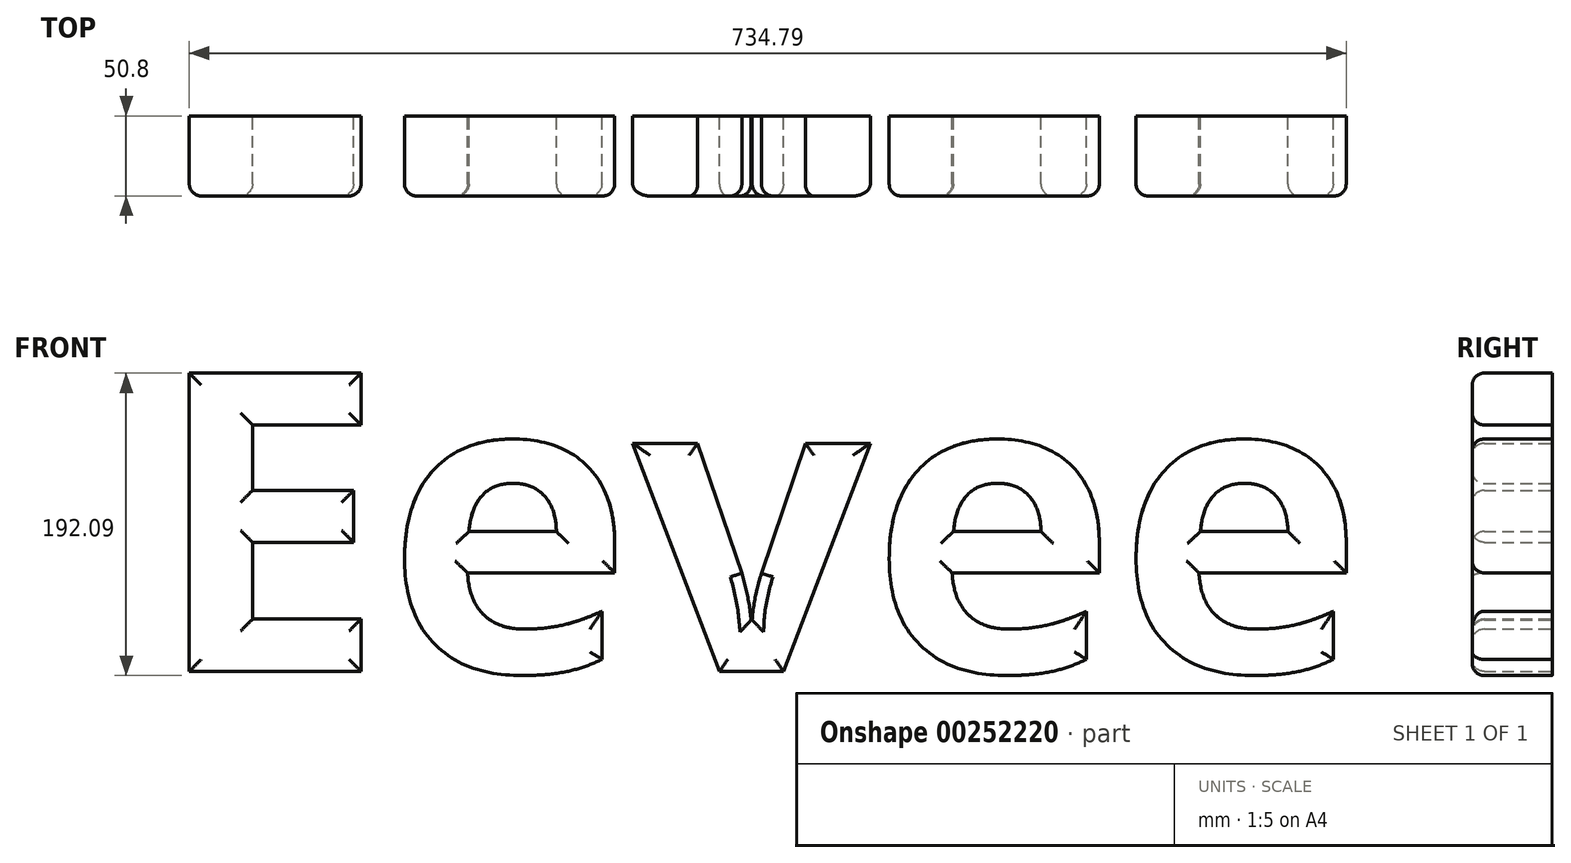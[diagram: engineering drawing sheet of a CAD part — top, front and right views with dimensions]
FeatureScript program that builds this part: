
annotation { "Feature Type Name" : "Feature", "Feature Type Description" : "" }
export const myFeature = defineFeature(function(context is Context, id is Id, definition is map)
    precondition{}
    {
        {
            var Q0;
            Q0=qCreatedBy(makeId("Front.planeOp"),FACE);
            var sketch = newSketch(context, id + "F0", { "sketchPlane" : qUnion([Q0])});
            skText(sketch, "E0", { "text": "Eevee", "fontName": "OpenSans-Bold.ttf"});
            const initialGuessF0  = {"E0": [-0.17, -0.0954, 1, 0, 0.1911]};
            skSetInitialGuess(sketch, initialGuessF0);
            skSolve(sketch);
        }
        {
            var Q0;
            Q0 = qSketchRegion(id + "F0", true);
            extrude(context, id + "F1", {"entities" : qUnion([Q0]), "depth" : 50.8 * mm});
        }
        {
            var Q0;
            Q0=makeQuery(id+"F1.opExtrude","CAP_FACE",FACE,{"disambiguationData":[OSD([sQuery(id+"F0.wireOp",EDGE,"E0.sketch_text.stroke-0"),sQuery(id+"F0.wireOp",EDGE,"E0.sketch_text.stroke-1"),sQuery(id+"F0.wireOp",EDGE,"E0.sketch_text.stroke-2"),sQuery(id+"F0.wireOp",EDGE,"E0.sketch_text.stroke-3"),sQuery(id+"F0.wireOp",EDGE,"E0.sketch_text.stroke-4"),sQuery(id+"F0.wireOp",EDGE,"E0.sketch_text.stroke-5"),sQuery(id+"F0.wireOp",EDGE,"E0.sketch_text.stroke-6"),sQuery(id+"F0.wireOp",EDGE,"E0.sketch_text.stroke-7"),sQuery(id+"F0.wireOp",EDGE,"E0.sketch_text.stroke-8"),sQuery(id+"F0.wireOp",EDGE,"E0.sketch_text.stroke-9"),sQuery(id+"F0.wireOp",EDGE,"E0.sketch_text.stroke-10"),sQuery(id+"F0.wireOp",EDGE,"E0.sketch_text.stroke-11")])],"isStart":false});
            var Q1;
            Q1=makeQuery(id+"F1.opExtrude","CAP_FACE",FACE,{"disambiguationData":[OSD([sQuery(id+"F0.wireOp",EDGE,"E0.sketch_text.stroke-12"),sQuery(id+"F0.wireOp",EDGE,"E0.sketch_text.stroke-13"),sQuery(id+"F0.wireOp",EDGE,"E0.sketch_text.stroke-14"),sQuery(id+"F0.wireOp",EDGE,"E0.sketch_text.stroke-15"),sQuery(id+"F0.wireOp",EDGE,"E0.sketch_text.stroke-16"),sQuery(id+"F0.wireOp",EDGE,"E0.sketch_text.stroke-17"),sQuery(id+"F0.wireOp",EDGE,"E0.sketch_text.stroke-18"),sQuery(id+"F0.wireOp",EDGE,"E0.sketch_text.stroke-19"),sQuery(id+"F0.wireOp",EDGE,"E0.sketch_text.stroke-20"),sQuery(id+"F0.wireOp",EDGE,"E0.sketch_text.stroke-21"),sQuery(id+"F0.wireOp",EDGE,"E0.sketch_text.stroke-22"),sQuery(id+"F0.wireOp",EDGE,"E0.sketch_text.stroke-23"),sQuery(id+"F0.wireOp",EDGE,"E0.sketch_text.stroke-24"),sQuery(id+"F0.wireOp",EDGE,"E0.sketch_text.stroke-25"),sQuery(id+"F0.wireOp",EDGE,"E0.sketch_text.stroke-26"),sQuery(id+"F0.wireOp",EDGE,"E0.sketch_text.stroke-27"),sQuery(id+"F0.wireOp",EDGE,"E0.sketch_text.stroke-28"),sQuery(id+"F0.wireOp",EDGE,"E0.sketch_text.stroke-29"),sQuery(id+"F0.wireOp",EDGE,"E0.sketch_text.stroke-30"),sQuery(id+"F0.wireOp",EDGE,"E0.sketch_text.stroke-31")])],"isStart":false});
            var Q2;
            Q2=makeQuery(id+"F1.opExtrude","CAP_FACE",FACE,{"disambiguationData":[OSD([sQuery(id+"F0.wireOp",EDGE,"E0.sketch_text.stroke-32"),sQuery(id+"F0.wireOp",EDGE,"E0.sketch_text.stroke-33"),sQuery(id+"F0.wireOp",EDGE,"E0.sketch_text.stroke-34"),sQuery(id+"F0.wireOp",EDGE,"E0.sketch_text.stroke-35"),sQuery(id+"F0.wireOp",EDGE,"E0.sketch_text.stroke-36"),sQuery(id+"F0.wireOp",EDGE,"E0.sketch_text.stroke-37"),sQuery(id+"F0.wireOp",EDGE,"E0.sketch_text.stroke-38"),sQuery(id+"F0.wireOp",EDGE,"E0.sketch_text.stroke-39"),sQuery(id+"F0.wireOp",EDGE,"E0.sketch_text.stroke-40"),sQuery(id+"F0.wireOp",EDGE,"E0.sketch_text.stroke-41")])],"isStart":false});
            var Q3;
            Q3=makeQuery(id+"F1.opExtrude","CAP_FACE",FACE,{"disambiguationData":[OSD([sQuery(id+"F0.wireOp",EDGE,"E0.sketch_text.stroke-42"),sQuery(id+"F0.wireOp",EDGE,"E0.sketch_text.stroke-43"),sQuery(id+"F0.wireOp",EDGE,"E0.sketch_text.stroke-44"),sQuery(id+"F0.wireOp",EDGE,"E0.sketch_text.stroke-45"),sQuery(id+"F0.wireOp",EDGE,"E0.sketch_text.stroke-46"),sQuery(id+"F0.wireOp",EDGE,"E0.sketch_text.stroke-47"),sQuery(id+"F0.wireOp",EDGE,"E0.sketch_text.stroke-48"),sQuery(id+"F0.wireOp",EDGE,"E0.sketch_text.stroke-49"),sQuery(id+"F0.wireOp",EDGE,"E0.sketch_text.stroke-50"),sQuery(id+"F0.wireOp",EDGE,"E0.sketch_text.stroke-51"),sQuery(id+"F0.wireOp",EDGE,"E0.sketch_text.stroke-52"),sQuery(id+"F0.wireOp",EDGE,"E0.sketch_text.stroke-53"),sQuery(id+"F0.wireOp",EDGE,"E0.sketch_text.stroke-54"),sQuery(id+"F0.wireOp",EDGE,"E0.sketch_text.stroke-55"),sQuery(id+"F0.wireOp",EDGE,"E0.sketch_text.stroke-56"),sQuery(id+"F0.wireOp",EDGE,"E0.sketch_text.stroke-57"),sQuery(id+"F0.wireOp",EDGE,"E0.sketch_text.stroke-58"),sQuery(id+"F0.wireOp",EDGE,"E0.sketch_text.stroke-59"),sQuery(id+"F0.wireOp",EDGE,"E0.sketch_text.stroke-60"),sQuery(id+"F0.wireOp",EDGE,"E0.sketch_text.stroke-61")])],"isStart":false});
            var Q4;
            Q4=makeQuery(id+"F1.opExtrude","CAP_FACE",FACE,{"disambiguationData":[OSD([sQuery(id+"F0.wireOp",EDGE,"E0.sketch_text.stroke-62"),sQuery(id+"F0.wireOp",EDGE,"E0.sketch_text.stroke-63"),sQuery(id+"F0.wireOp",EDGE,"E0.sketch_text.stroke-64"),sQuery(id+"F0.wireOp",EDGE,"E0.sketch_text.stroke-65"),sQuery(id+"F0.wireOp",EDGE,"E0.sketch_text.stroke-66"),sQuery(id+"F0.wireOp",EDGE,"E0.sketch_text.stroke-67"),sQuery(id+"F0.wireOp",EDGE,"E0.sketch_text.stroke-68"),sQuery(id+"F0.wireOp",EDGE,"E0.sketch_text.stroke-69"),sQuery(id+"F0.wireOp",EDGE,"E0.sketch_text.stroke-70"),sQuery(id+"F0.wireOp",EDGE,"E0.sketch_text.stroke-71"),sQuery(id+"F0.wireOp",EDGE,"E0.sketch_text.stroke-72"),sQuery(id+"F0.wireOp",EDGE,"E0.sketch_text.stroke-73"),sQuery(id+"F0.wireOp",EDGE,"E0.sketch_text.stroke-74"),sQuery(id+"F0.wireOp",EDGE,"E0.sketch_text.stroke-75"),sQuery(id+"F0.wireOp",EDGE,"E0.sketch_text.stroke-76"),sQuery(id+"F0.wireOp",EDGE,"E0.sketch_text.stroke-77"),sQuery(id+"F0.wireOp",EDGE,"E0.sketch_text.stroke-78"),sQuery(id+"F0.wireOp",EDGE,"E0.sketch_text.stroke-79"),sQuery(id+"F0.wireOp",EDGE,"E0.sketch_text.stroke-80"),sQuery(id+"F0.wireOp",EDGE,"E0.sketch_text.stroke-81")])],"isStart":false});
            fillet(context, id + "F2", {"entities" : qUnion([Q0, Q1, Q2, Q3, Q4]), "radius" : 7.62 * mm, "tangentPropagation" : true, "allowEdgeOverflow" : false});
        }
    });
